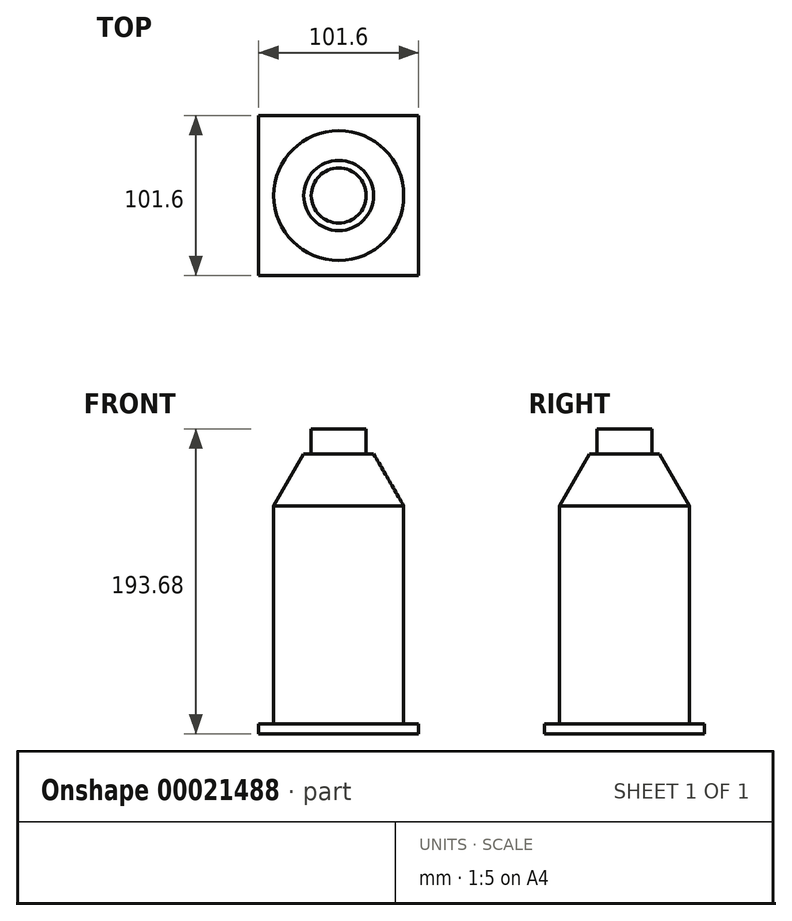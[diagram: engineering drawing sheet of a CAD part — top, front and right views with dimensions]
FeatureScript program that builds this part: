
annotation { "Feature Type Name" : "Feature", "Feature Type Description" : "" }
export const myFeature = defineFeature(function(context is Context, id is Id, definition is map)
    precondition{}
    {
        {
            var Q0;
            Q0=qCreatedBy(makeId("Top.planeOp"),FACE);
            var sketch = newSketch(context, id + "F0", { "sketchPlane" : qUnion([Q0])});
            skLineSegment(sketch, "E0.rect.bottom", {"start": v(50.8, -50.8) * mm, "end": v(-50.8, -50.8) * mm});
            skLineSegment(sketch, "E0.rect.top", {"start": v(50.8, 50.8) * mm, "end": v(-50.8, 50.8) * mm});
            skLineSegment(sketch, "E0.rect.left", {"start": v(50.8, -50.8) * mm, "end": v(50.8, 50.8) * mm});
            skLineSegment(sketch, "E0.rect.right", {"start": v(-50.8, -50.8) * mm, "end": v(-50.8, 50.8) * mm});
            skPoint(sketch, "E0.rect.middle", {"position": v(0, 0) * mm});
            skCircle(sketch, "E1", {"center": v(0, 0) * mm, "radius": 41.28 * mm});
            skSolve(sketch);
        }
        {
            var Q0;
            Q0=qSketchRegion(id+"F0",true);
            var Q1;
            Q1=makeQuery(id+"F0.imprint","IMPRINT",FACE,{"disambiguationData":[TD([[makeQuery(id+"F0.imprint","IMPRINT",EDGE,{"derivedFrom":sQuery(id+"F0.wireOp",EDGE,"E1")}),1.0]])]});
            extrude(context, id + "F1", {"entities" : qUnion([Q0, Q1]), "depth" : 6.35 * mm});
        }
        {
            var Q0;
            Q0=makeQuery(id+"F0.imprint","IMPRINT",FACE,{"disambiguationData":[TD([[makeQuery(id+"F0.imprint","IMPRINT",EDGE,{"derivedFrom":sQuery(id+"F0.wireOp",EDGE,"E1")}),1.0]])]});
            extrude(context, id + "F2", {"entities" : qUnion([Q0]), "operationType" : NewBodyOperationType.ADD, "depth" : 177.8 * mm});
        }
        {
            var Q0;
            Q0=makeQuery(id+"F2.opExtrude","CAP_EDGE",EDGE,{"disambiguationData":[OSD([sQuery(id+"F0.wireOp",EDGE,"E1")])],"isStart":false});
            chamfer(context, id + "F3", {"entities" : qUnion([Q0]), "chamferType" : ChamferType.OFFSET_ANGLE, "width" : 19.05 * mm, "oppositeDirection" : false, "angle" : 60 * degree, "tangentPropagation" : true});
        }
        {
            var Q0;
            Q0=makeQuery(id+"F2.opExtrude","CAP_FACE",FACE,{"disambiguationData":[OSD([sQuery(id+"F0.wireOp",EDGE,"E1")])],"isStart":false});
            var sketch = newSketch(context, id + "F4", { "sketchPlane" : qUnion([Q0])});
            skCircle(sketch, "E2", {"center": v(0, 0) * mm, "radius": 17.46 * mm});
            skSolve(sketch);
        }
        {
            var Q0;
            Q0=qSketchRegion(id+"F4",true);
            extrude(context, id + "F5", {"entities" : qUnion([Q0]), "operationType" : NewBodyOperationType.ADD, "depth" : 15.88 * mm});
        }
    });
